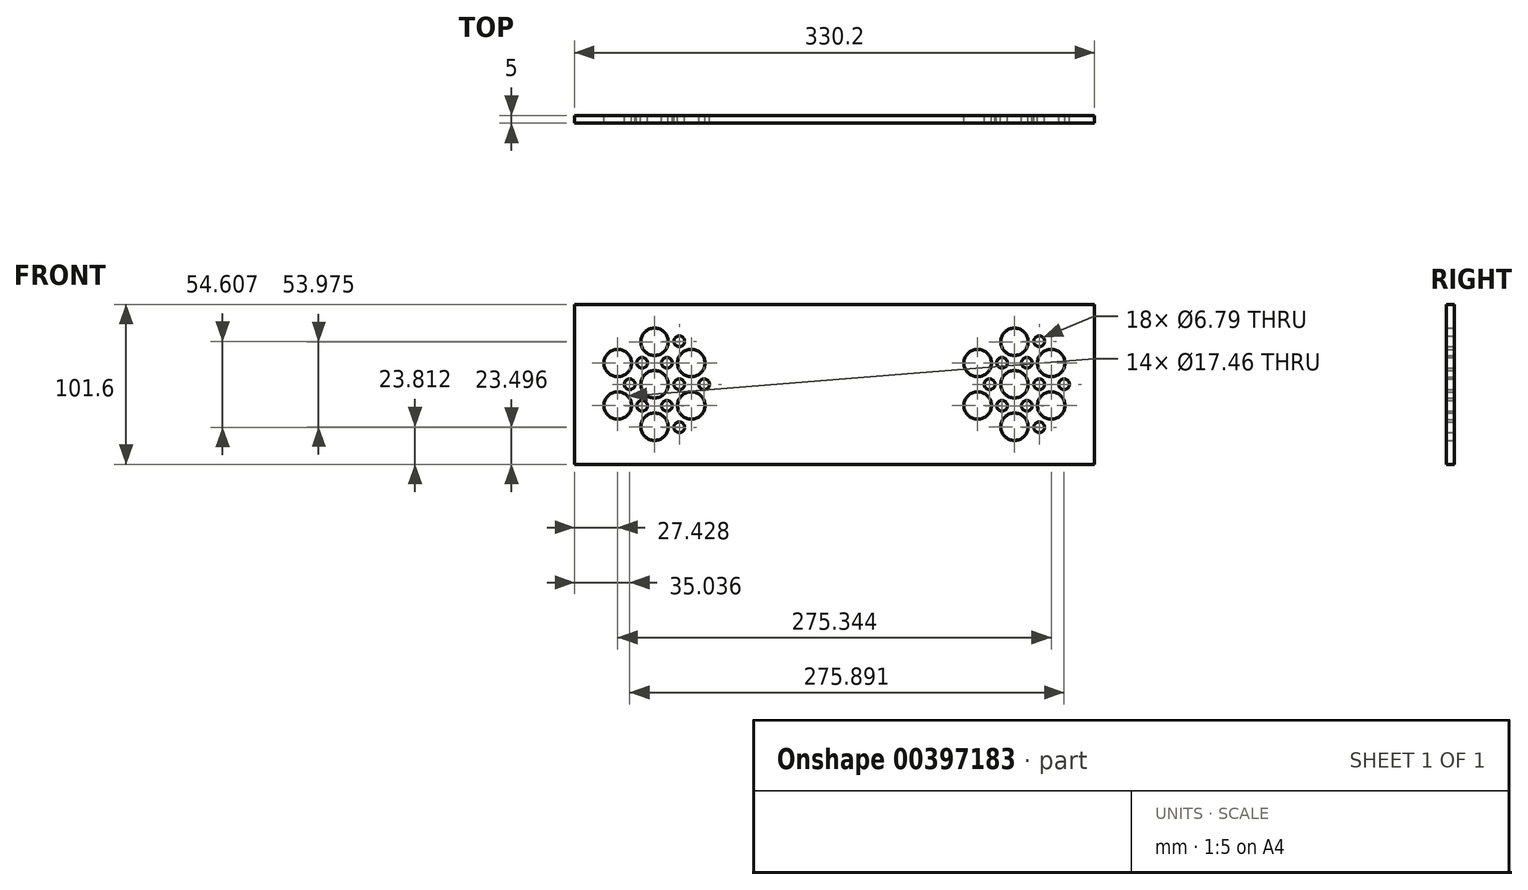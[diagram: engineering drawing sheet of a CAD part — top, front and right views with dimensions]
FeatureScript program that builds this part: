
annotation { "Feature Type Name" : "Feature", "Feature Type Description" : "" }
export const myFeature = defineFeature(function(context is Context, id is Id, definition is map)
    precondition{}
    {
        {
            var Q0;
            Q0=qCreatedBy(makeId("Front.planeOp"),FACE);
            var sketch = newSketch(context, id + "F0", { "sketchPlane" : qUnion([Q0])});
            skLineSegment(sketch, "E0.bottom", {"start": v(47.62, -47.62) * mm, "end": v(-47.62, -47.63) * mm});
            skLineSegment(sketch, "E0.top", {"start": v(47.62, 47.63) * mm, "end": v(-47.62, 47.63) * mm});
            skLineSegment(sketch, "E0.left", {"start": v(47.63, -47.62) * mm, "end": v(47.63, 47.62) * mm});
            skLineSegment(sketch, "E0.right", {"start": v(-47.63, -47.62) * mm, "end": v(-47.63, 47.62) * mm});
            skPoint(sketch, "E0.middle", {"position": v(0, 0) * mm});
            skCircle(sketch, "E1", {"center": v(0, 26.99) * mm, "radius": 8.73 * mm});
            skCircle(sketch, "E2", {"center": v(0, 0) * mm, "radius": 35.72 * mm, "construction": true});
            skCircle(sketch, "E3.1.0", {"center": v(-23.37, 13.5) * mm, "radius": 8.73 * mm});
            skCircle(sketch, "E3.2.0", {"center": v(-23.37, -13.5) * mm, "radius": 8.73 * mm});
            skCircle(sketch, "E4.1.3.0", {"center": v(0, -26.99) * mm, "radius": 8.73 * mm});
            skCircle(sketch, "E4.1.4.0", {"center": v(23.37, -13.5) * mm, "radius": 8.73 * mm});
            skCircle(sketch, "E4.1.5.0", {"center": v(23.37, 13.5) * mm, "radius": 8.73 * mm});
            skCircle(sketch, "E5", {"center": v(0, 0) * mm, "radius": 8.73 * mm});
            skSolve(sketch);
        }
        {
            var Q0;
            Q0=qCreatedBy(makeId("Front.planeOp"),FACE);
            var sketch = newSketch(context, id + "F1", { "sketchPlane" : qUnion([Q0])});
            skLineSegment(sketch, "E6.bottom", {"start": v(165.1, -50.8) * mm, "end": v(-165.1, -50.8) * mm});
            skLineSegment(sketch, "E6.top", {"start": v(165.1, 50.8) * mm, "end": v(-165.1, 50.8) * mm});
            skLineSegment(sketch, "E6.left", {"start": v(165.1, -50.8) * mm, "end": v(165.1, 50.8) * mm});
            skLineSegment(sketch, "E6.right", {"start": v(-165.1, -50.8) * mm, "end": v(-165.1, 50.8) * mm});
            skPoint(sketch, "E6.middle", {"position": v(0, 0) * mm});
            skCircle(sketch, "E7.5", {"center": v(0, 26.99) * mm, "radius": 8.73 * mm, "construction": true});
            skCircle(sketch, "E7.7", {"center": v(-23.37, 13.5) * mm, "radius": 8.73 * mm, "construction": true});
            skCircle(sketch, "E7.8", {"center": v(-23.37, -13.5) * mm, "radius": 8.73 * mm, "construction": true});
            skCircle(sketch, "E7.10", {"center": v(0, -26.99) * mm, "radius": 8.73 * mm, "construction": true});
            skCircle(sketch, "E7.11", {"center": v(23.37, -13.5) * mm, "radius": 8.73 * mm, "construction": true});
            skCircle(sketch, "E7.12", {"center": v(23.37, 13.5) * mm, "radius": 8.73 * mm, "construction": true});
            skCircle(sketch, "E7.13", {"center": v(0, -31.53) * mm, "radius": 3.4 * mm, "construction": true});
            skCircle(sketch, "E7.14", {"center": v(15.76, -27.3) * mm, "radius": 3.4 * mm, "construction": true});
            skCircle(sketch, "E7.15", {"center": v(27.3, -15.76) * mm, "radius": 3.4 * mm, "construction": true});
            skCircle(sketch, "E7.16", {"center": v(31.53, 0) * mm, "radius": 3.4 * mm, "construction": true});
            skCircle(sketch, "E7.17", {"center": v(-7.88, 13.65) * mm, "radius": 3.4 * mm, "construction": true});
            skCircle(sketch, "E7.18", {"center": v(-15.76, 0) * mm, "radius": 3.4 * mm, "construction": true});
            skCircle(sketch, "E7.19", {"center": v(-7.88, -13.65) * mm, "radius": 3.4 * mm, "construction": true});
            skCircle(sketch, "E7.21", {"center": v(7.88, -13.65) * mm, "radius": 3.4 * mm, "construction": true});
            skCircle(sketch, "E7.22", {"center": v(15.76, 0) * mm, "radius": 3.4 * mm, "construction": true});
            skCircle(sketch, "E7.23", {"center": v(0, 0) * mm, "radius": 8.73 * mm, "construction": true});
            skCircle(sketch, "E7.24", {"center": v(27.3, 15.76) * mm, "radius": 3.4 * mm, "construction": true});
            skCircle(sketch, "E7.25", {"center": v(15.76, 27.3) * mm, "radius": 3.4 * mm, "construction": true});
            skCircle(sketch, "E7.26", {"center": v(7.88, 13.65) * mm, "radius": 3.4 * mm, "construction": true});
            skLineSegment(sketch, "E8", {"start": v(114.3, 50.8) * mm, "end": v(114.3, -50.8) * mm, "construction": true});
            skLineSegment(sketch, "E9", {"start": v(114.3, 0) * mm, "end": v(165.1, 0) * mm, "construction": true});
            skCircle(sketch, "E10.1.0.0", {"center": v(122.18, 13.65) * mm, "radius": 3.4 * mm});
            skCircle(sketch, "E10.1.0.1", {"center": v(130.06, 27.3) * mm, "radius": 3.4 * mm});
            skCircle(sketch, "E10.1.0.2", {"center": v(106.42, -13.65) * mm, "radius": 3.4 * mm});
            skCircle(sketch, "E10.1.0.3", {"center": v(106.42, 13.65) * mm, "radius": 3.4 * mm});
            skCircle(sketch, "E10.1.0.4", {"center": v(145.83, 0) * mm, "radius": 3.4 * mm});
            skCircle(sketch, "E10.1.0.5", {"center": v(130.06, 0) * mm, "radius": 3.4 * mm});
            skCircle(sketch, "E10.1.0.6", {"center": v(141.6, -15.76) * mm, "radius": 3.4 * mm});
            skCircle(sketch, "E10.1.0.7", {"center": v(122.18, -13.65) * mm, "radius": 3.4 * mm});
            skPoint(sketch, "E10.1.0.8", {"position": v(114.3, 0) * mm});
            skCircle(sketch, "E10.1.0.9", {"center": v(130.06, -27.3) * mm, "radius": 3.4 * mm});
            skCircle(sketch, "E10.1.0.10", {"center": v(114.3, -31.53) * mm, "radius": 3.4 * mm});
            skCircle(sketch, "E10.1.0.11", {"center": v(137.67, 13.5) * mm, "radius": 8.73 * mm});
            skCircle(sketch, "E10.1.0.12", {"center": v(137.67, -13.5) * mm, "radius": 8.73 * mm});
            skCircle(sketch, "E10.1.0.13", {"center": v(141.6, 15.76) * mm, "radius": 3.4 * mm});
            skCircle(sketch, "E10.1.0.14", {"center": v(114.3, -26.99) * mm, "radius": 8.73 * mm});
            skCircle(sketch, "E10.1.0.15", {"center": v(90.93, -13.5) * mm, "radius": 8.73 * mm});
            skCircle(sketch, "E10.1.0.16", {"center": v(90.93, 13.5) * mm, "radius": 8.73 * mm});
            skCircle(sketch, "E10.1.0.17", {"center": v(114.3, 26.99) * mm, "radius": 8.73 * mm});
            skCircle(sketch, "E10.1.0.18", {"center": v(98.54, 0) * mm, "radius": 3.4 * mm});
            skPoint(sketch, "E10.1.0.19", {"position": v(114.3, 0) * mm});
            skPoint(sketch, "E10.1.0.20", {"position": v(114.3, 0) * mm});
            skPoint(sketch, "E10.1.0.21", {"position": v(114.3, 0) * mm});
            skCircle(sketch, "E10.1.0.22", {"center": v(114.3, 0) * mm, "radius": 8.73 * mm});
            skLineSegment(sketch, "E10.direction1", {"start": v(23.37, 13.5) * mm, "end": v(137.67, 13.5) * mm, "construction": true});
            skCircle(sketch, "E11.1.0.0", {"center": v(-98.54, 0) * mm, "radius": 3.4 * mm});
            skCircle(sketch, "E11.1.0.1", {"center": v(-122.18, -13.65) * mm, "radius": 3.4 * mm});
            skCircle(sketch, "E11.1.0.2", {"center": v(-87, -15.76) * mm, "radius": 3.4 * mm});
            skPoint(sketch, "E11.1.0.3", {"position": v(-114.3, 0) * mm});
            skCircle(sketch, "E11.1.0.4", {"center": v(-106.42, 13.65) * mm, "radius": 3.4 * mm});
            skCircle(sketch, "E11.1.0.5", {"center": v(-82.77, 0) * mm, "radius": 3.4 * mm});
            skCircle(sketch, "E11.1.0.6", {"center": v(-122.18, 13.65) * mm, "radius": 3.4 * mm});
            skCircle(sketch, "E11.1.0.7", {"center": v(-130.06, 0) * mm, "radius": 3.4 * mm});
            skCircle(sketch, "E11.1.0.8", {"center": v(-114.3, 0) * mm, "radius": 8.73 * mm});
            skCircle(sketch, "E11.1.0.9", {"center": v(-98.54, 27.3) * mm, "radius": 3.4 * mm});
            skCircle(sketch, "E11.1.0.10", {"center": v(-114.3, 26.99) * mm, "radius": 8.73 * mm});
            skCircle(sketch, "E11.1.0.11", {"center": v(-137.67, 13.5) * mm, "radius": 8.73 * mm});
            skCircle(sketch, "E11.1.0.12", {"center": v(-137.67, -13.5) * mm, "radius": 8.73 * mm});
            skCircle(sketch, "E11.1.0.13", {"center": v(-114.3, -26.99) * mm, "radius": 8.73 * mm});
            skCircle(sketch, "E11.1.0.14", {"center": v(-87, 15.76) * mm, "radius": 3.4 * mm});
            skCircle(sketch, "E11.1.0.15", {"center": v(-90.93, -13.5) * mm, "radius": 8.73 * mm});
            skCircle(sketch, "E11.1.0.16", {"center": v(-90.93, 13.5) * mm, "radius": 8.73 * mm});
            skCircle(sketch, "E11.1.0.17", {"center": v(-114.3, -31.53) * mm, "radius": 3.4 * mm});
            skCircle(sketch, "E11.1.0.18", {"center": v(-98.54, -27.3) * mm, "radius": 3.4 * mm});
            skCircle(sketch, "E11.1.0.19", {"center": v(-106.42, -13.65) * mm, "radius": 3.4 * mm});
            skPoint(sketch, "E11.1.0.20", {"position": v(-114.3, 0) * mm});
            skPoint(sketch, "E11.1.0.21", {"position": v(-114.3, 0) * mm});
            skPoint(sketch, "E11.1.0.22", {"position": v(-114.3, 0) * mm});
            skLineSegment(sketch, "E11.direction1", {"start": v(23.37, 13.5) * mm, "end": v(-90.93, 13.5) * mm, "construction": true});
            skLineSegment(sketch, "E12", {"start": v(-114.3, 50.8) * mm, "end": v(-114.3, -50.8) * mm, "construction": true});
            skLineSegment(sketch, "E13", {"start": v(-114.3, 0) * mm, "end": v(-165.1, 0) * mm, "construction": true});
            skLineSegment(sketch, "E14", {"start": v(0, 50.8) * mm, "end": v(0, -50.8) * mm, "construction": true});
            skSolve(sketch);
        }
        {
            var Q0;
            Q0 = qSketchRegion(id + "F1", true);
            extrude(context, id + "F2", {"entities" : qUnion([Q0]), "depth" : 5 * mm});
        }
    });
